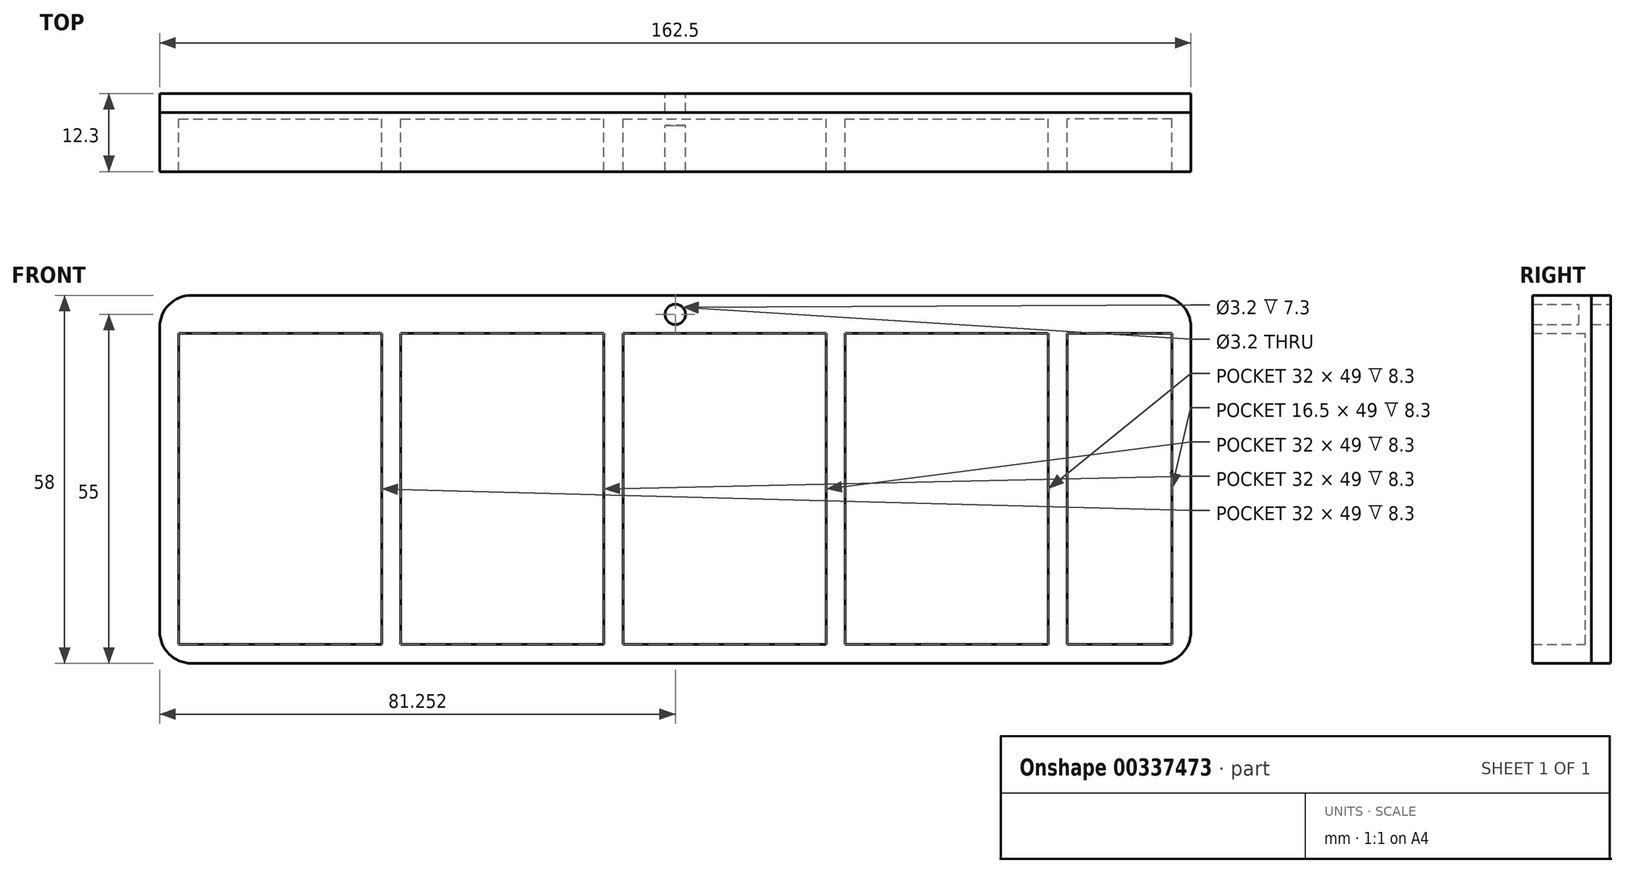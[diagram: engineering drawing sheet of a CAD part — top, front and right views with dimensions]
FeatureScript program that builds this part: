
annotation { "Feature Type Name" : "Feature", "Feature Type Description" : "" }
export const myFeature = defineFeature(function(context is Context, id is Id, definition is map)
    precondition{}
    {
        {
            var Q0;
            Q0=qCreatedBy(makeId("Front.planeOp"),FACE);
            var sketch = newSketch(context, id + "F0", { "sketchPlane" : qUnion([Q0])});
            skLineSegment(sketch, "E0", {"start": v(-131.97, 0) * mm, "end": v(-99.97, 0) * mm});
            skLineSegment(sketch, "E1", {"start": v(-99.97, 0) * mm, "end": v(-99.97, 49) * mm});
            skLineSegment(sketch, "E2", {"start": v(-99.97, 49) * mm, "end": v(-131.97, 49) * mm});
            skLineSegment(sketch, "E3", {"start": v(-131.97, 49) * mm, "end": v(-131.97, 0) * mm});
            skLineSegment(sketch, "E4", {"start": v(-96.97, 0) * mm, "end": v(-96.97, 49) * mm});
            skLineSegment(sketch, "E5", {"start": v(-96.97, 49) * mm, "end": v(-80.47, 49) * mm});
            skLineSegment(sketch, "E6", {"start": v(-80.47, 49) * mm, "end": v(-80.47, 0) * mm});
            skLineSegment(sketch, "E7", {"start": v(-80.47, 0) * mm, "end": v(-96.97, 0) * mm});
            skLineSegment(sketch, "E8", {"start": v(-134.97, 0) * mm, "end": v(-134.97, 49) * mm});
            skLineSegment(sketch, "E9", {"start": v(-134.97, 49) * mm, "end": v(-166.97, 49) * mm});
            skLineSegment(sketch, "E10", {"start": v(-166.97, 49) * mm, "end": v(-166.97, 0) * mm});
            skLineSegment(sketch, "E11", {"start": v(-166.97, 0) * mm, "end": v(-134.97, 0) * mm});
            skLineSegment(sketch, "E12", {"start": v(-169.97, 0) * mm, "end": v(-169.97, 49) * mm});
            skLineSegment(sketch, "E13", {"start": v(-169.97, 49) * mm, "end": v(-201.97, 49) * mm});
            skLineSegment(sketch, "E14", {"start": v(-201.97, 49) * mm, "end": v(-201.97, 0) * mm});
            skLineSegment(sketch, "E15", {"start": v(-201.97, 0) * mm, "end": v(-169.97, 0) * mm});
            skLineSegment(sketch, "E16", {"start": v(-204.97, 0) * mm, "end": v(-204.97, 49) * mm});
            skLineSegment(sketch, "E17", {"start": v(-204.97, 49) * mm, "end": v(-236.97, 49) * mm});
            skLineSegment(sketch, "E18", {"start": v(-236.97, 49) * mm, "end": v(-236.97, 0) * mm});
            skLineSegment(sketch, "E19", {"start": v(-236.97, 0) * mm, "end": v(-204.97, 0) * mm});
            skLineSegment(sketch, "E20", {"start": v(-239.97, 55) * mm, "end": v(-77.47, 55) * mm});
            skLineSegment(sketch, "E21", {"start": v(-77.47, 55) * mm, "end": v(-77.47, -3) * mm});
            skLineSegment(sketch, "E22", {"start": v(-77.47, -3) * mm, "end": v(-239.97, -3) * mm});
            skLineSegment(sketch, "E23", {"start": v(-239.97, -3) * mm, "end": v(-239.97, 55) * mm});
            skLineSegment(sketch, "E24", {"start": v(-158.72, 55) * mm, "end": v(-158.72, 52) * mm, "construction": true});
            skCircle(sketch, "E25", {"center": v(-158.72, 52) * mm, "radius": 1.6 * mm});
            skSolve(sketch);
        }
        {
            var Q0;
            Q0 = qSketchRegion(id + "F0", true);
            extrude(context, id + "F1", {"entities" : qUnion([Q0]), "depth" : 12.3 * mm});
        }
        {
            var Q0;
            Q0=makeQuery(id+"F0.imprint","IMPRINT",FACE,{"disambiguationData":[TD([[makeQuery(id+"F0.imprint","IMPRINT",EDGE,{"derivedFrom":sQuery(id+"F0.wireOp",EDGE,"E16")}),1.0]])]});
            var Q1;
            Q1=makeQuery(id+"F0.imprint","IMPRINT",FACE,{"disambiguationData":[TD([[makeQuery(id+"F0.imprint","IMPRINT",EDGE,{"derivedFrom":sQuery(id+"F0.wireOp",EDGE,"E12")}),1.0]])]});
            var Q2;
            Q2=makeQuery(id+"F0.imprint","IMPRINT",FACE,{"disambiguationData":[TD([[makeQuery(id+"F0.imprint","IMPRINT",EDGE,{"derivedFrom":sQuery(id+"F0.wireOp",EDGE,"E8")}),1.0]])]});
            var Q3;
            Q3=makeQuery(id+"F0.imprint","IMPRINT",FACE,{"disambiguationData":[TD([[makeQuery(id+"F0.imprint","IMPRINT",EDGE,{"derivedFrom":sQuery(id+"F0.wireOp",EDGE,"E0")}),1.0]])]});
            var Q4;
            Q4=makeQuery(id+"F0.imprint","IMPRINT",FACE,{"disambiguationData":[TD([[makeQuery(id+"F0.imprint","IMPRINT",EDGE,{"derivedFrom":sQuery(id+"F0.wireOp",EDGE,"E4")}),-1.0]])]});
            extrude(context, id + "F2", {"entities" : qUnion([Q0, Q1, Q2, Q3, Q4]), "operationType" : NewBodyOperationType.ADD, "depth" : 4 * mm});
        }
        {
            var Q0;
            Q0=makeQuery(id+"F0.imprint","IMPRINT",FACE,{"disambiguationData":[TD([[makeQuery(id+"F0.imprint","IMPRINT",EDGE,{"derivedFrom":sQuery(id+"F0.wireOp",EDGE,"E25")}),1.0]])]});
            extrude(context, id + "F3", {"entities" : qUnion([Q0]), "operationType" : NewBodyOperationType.ADD, "depth" : 5 * mm});
        }
        {
            var Q0;
            Q0=makeQuery(id+"F1.opExtrude","SWEPT_EDGE",EDGE,{"disambiguationData":[OSD([sQuery(id+"F0.wireOp",EDGE,"E21"),sQuery(id+"F0.wireOp",EDGE,"E22")])]});
            var Q1;
            Q1=makeQuery(id+"F1.opExtrude","SWEPT_EDGE",EDGE,{"disambiguationData":[OSD([sQuery(id+"F0.wireOp",EDGE,"E20"),sQuery(id+"F0.wireOp",EDGE,"E21")])]});
            var Q2;
            Q2=makeQuery(id+"F1.opExtrude","SWEPT_EDGE",EDGE,{"disambiguationData":[OSD([sQuery(id+"F0.wireOp",EDGE,"E22"),sQuery(id+"F0.wireOp",EDGE,"E23")])]});
            var Q3;
            Q3=makeQuery(id+"F1.opExtrude","SWEPT_EDGE",EDGE,{"disambiguationData":[OSD([sQuery(id+"F0.wireOp",EDGE,"E20"),sQuery(id+"F0.wireOp",EDGE,"E23")])]});
            fillet(context, id + "F4", {"entities" : qUnion([Q0, Q1, Q2, Q3]), "radius" : 5 * mm, "tangentPropagation" : true, "allowEdgeOverflow" : false});
        }
        {
            var Q0;
            Q0=qCreatedBy(makeId("Front.planeOp"),FACE);
            var sketch = newSketch(context, id + "F5", { "sketchPlane" : qUnion([Q0])});
            skArc(sketch, "E26.0", {"start": v(-234.97, 55) * mm, "mid": v(-238.5, 53.54) * mm, "end": v(-239.97, 50) * mm});
            skLineSegment(sketch, "E27.0", {"start": v(-234.97, 55) * mm, "end": v(-82.47, 55) * mm});
            skCircle(sketch, "E28.0", {"center": v(-158.72, 52) * mm, "radius": 1.6 * mm});
            skArc(sketch, "E29.0", {"start": v(-77.47, 50) * mm, "mid": v(-78.93, 53.54) * mm, "end": v(-82.47, 55) * mm});
            skLineSegment(sketch, "E30.0", {"start": v(-77.47, 50) * mm, "end": v(-77.47, 2) * mm});
            skArc(sketch, "E31.0", {"start": v(-82.47, -3) * mm, "mid": v(-78.93, -1.54) * mm, "end": v(-77.47, 2) * mm});
            skLineSegment(sketch, "E32.0", {"start": v(-82.47, -3) * mm, "end": v(-234.97, -3) * mm});
            skArc(sketch, "E33.0", {"start": v(-239.97, 2) * mm, "mid": v(-238.5, -1.54) * mm, "end": v(-234.97, -3) * mm});
            skLineSegment(sketch, "E34.0", {"start": v(-239.97, 2) * mm, "end": v(-239.97, 50) * mm});
            skSolve(sketch);
        }
        {
            var Q0;
            Q0=makeQuery(id+"F5.imprint","IMPRINT",FACE,{"disambiguationData":[TD([[makeQuery(id+"F5.imprint","IMPRINT",EDGE,{"derivedFrom":sQuery(id+"F5.wireOp",EDGE,"E26.0")}),1.0]])]});
            extrude(context, id + "F6", {"entities" : qUnion([Q0]), "depth" : 3 * mm});
        }
    });
